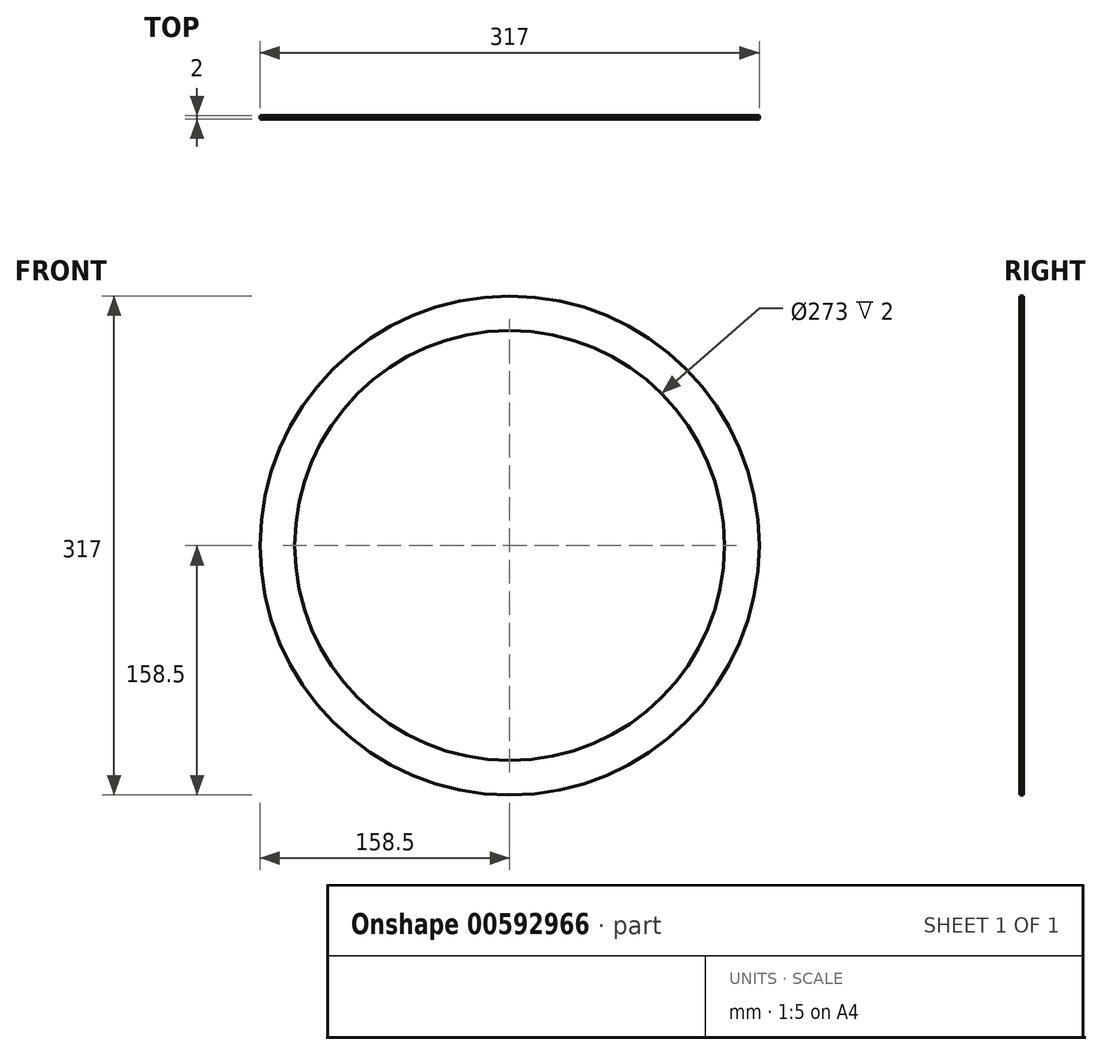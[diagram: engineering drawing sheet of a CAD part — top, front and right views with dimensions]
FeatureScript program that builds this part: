
annotation { "Feature Type Name" : "Feature", "Feature Type Description" : "" }
export const myFeature = defineFeature(function(context is Context, id is Id, definition is map)
    precondition{}
    {
        {
            var Q0;
            Q0=qCreatedBy(makeId("Front.planeOp"),FACE);
            var sketch = newSketch(context, id + "F0", { "sketchPlane" : qUnion([Q0])});
            skCircle(sketch, "E0", {"center": v(0, 0) * mm, "radius": 136.5 * mm});
            skCircle(sketch, "E1", {"center": v(0, 0) * mm, "radius": 158.5 * mm});
            skSolve(sketch);
        }
        {
            var Q0;
            Q0=makeQuery(id+"F0.imprint","IMPRINT",FACE,{"disambiguationData":[TD([[makeQuery(id+"F0.imprint","IMPRINT",EDGE,{"derivedFrom":sQuery(id+"F0.wireOp",EDGE,"E0")}),-1.0]])]});
            extrude(context, id + "F1", {"entities" : qUnion([Q0]), "endBound" : BoundingType.SYMMETRIC, "depth" : 2 * mm, "offsetDistance" : 25 * mm});
        }
    });
